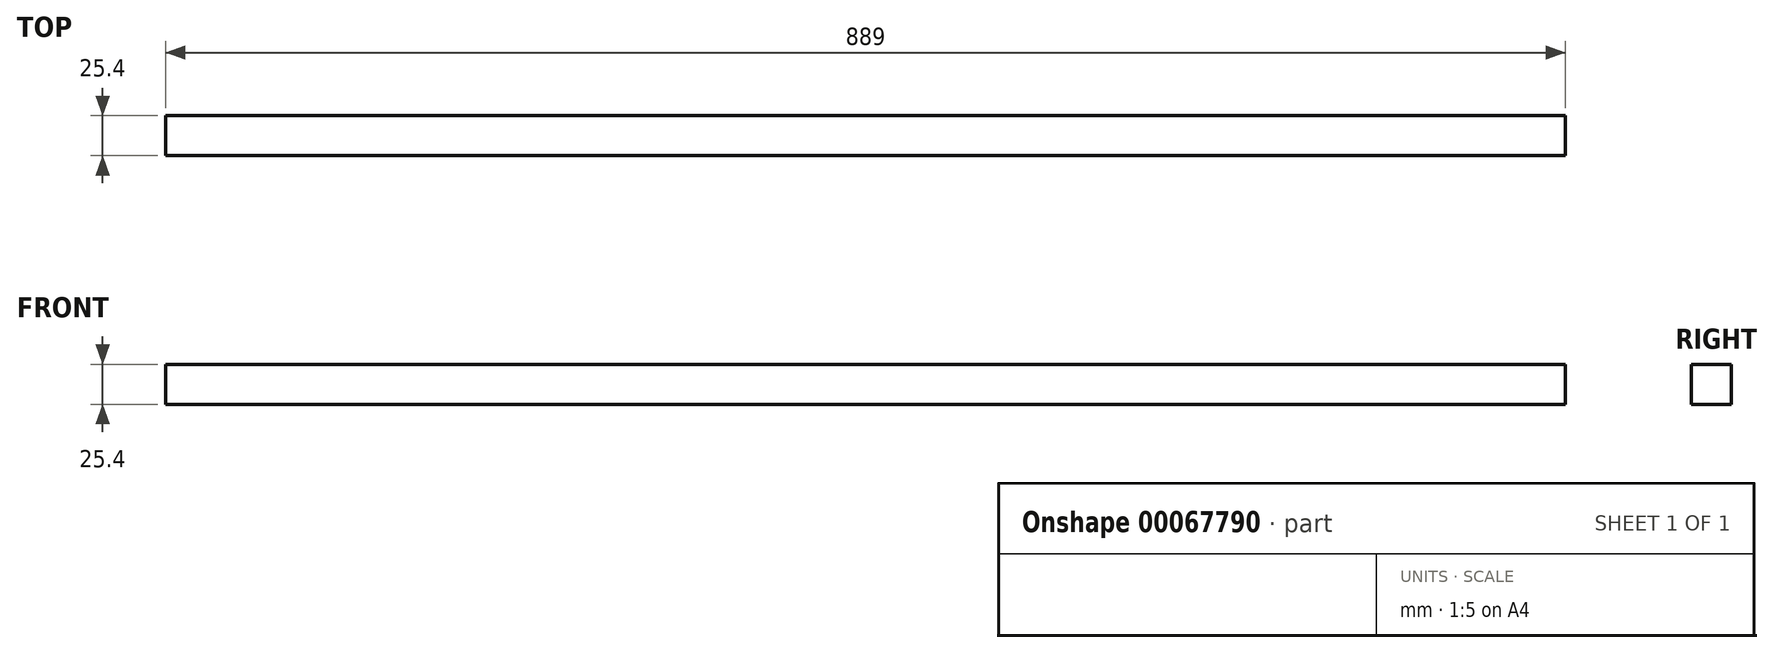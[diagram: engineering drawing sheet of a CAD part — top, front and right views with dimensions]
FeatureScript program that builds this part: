
annotation { "Feature Type Name" : "Feature", "Feature Type Description" : "" }
export const myFeature = defineFeature(function(context is Context, id is Id, definition is map)
    precondition{}
    {
        {
            var Q0;
            Q0=qCreatedBy(makeId("Right.planeOp"),FACE);
            var sketch = newSketch(context, id + "F0", { "sketchPlane" : qUnion([Q0])});
            skLineSegment(sketch, "E0.bottom", {"start": v(-12.7, 12.7) * mm, "end": v(12.7, 12.7) * mm});
            skLineSegment(sketch, "E0.top", {"start": v(-12.7, -12.7) * mm, "end": v(12.7, -12.7) * mm});
            skLineSegment(sketch, "E0.left", {"start": v(12.7, 12.7) * mm, "end": v(12.7, -12.7) * mm});
            skLineSegment(sketch, "E0.right", {"start": v(-12.7, 12.7) * mm, "end": v(-12.7, -12.7) * mm});
            skPoint(sketch, "E1", {"position": v(0, 0) * mm});
            skPoint(sketch, "E2.orphan", {"position": v(0, 12.7) * mm});
            skPoint(sketch, "E3.end.orphan", {"position": v(0, -12.7) * mm});
            skSolve(sketch);
        }
        {
            var Q0;
            Q0 = qSketchRegion(id + "F0", true);
            extrude(context, id + "F1", {"entities" : qUnion([Q0]), "endBound" : BoundingType.SYMMETRIC, "depth" : 889 * mm});
        }
    });
